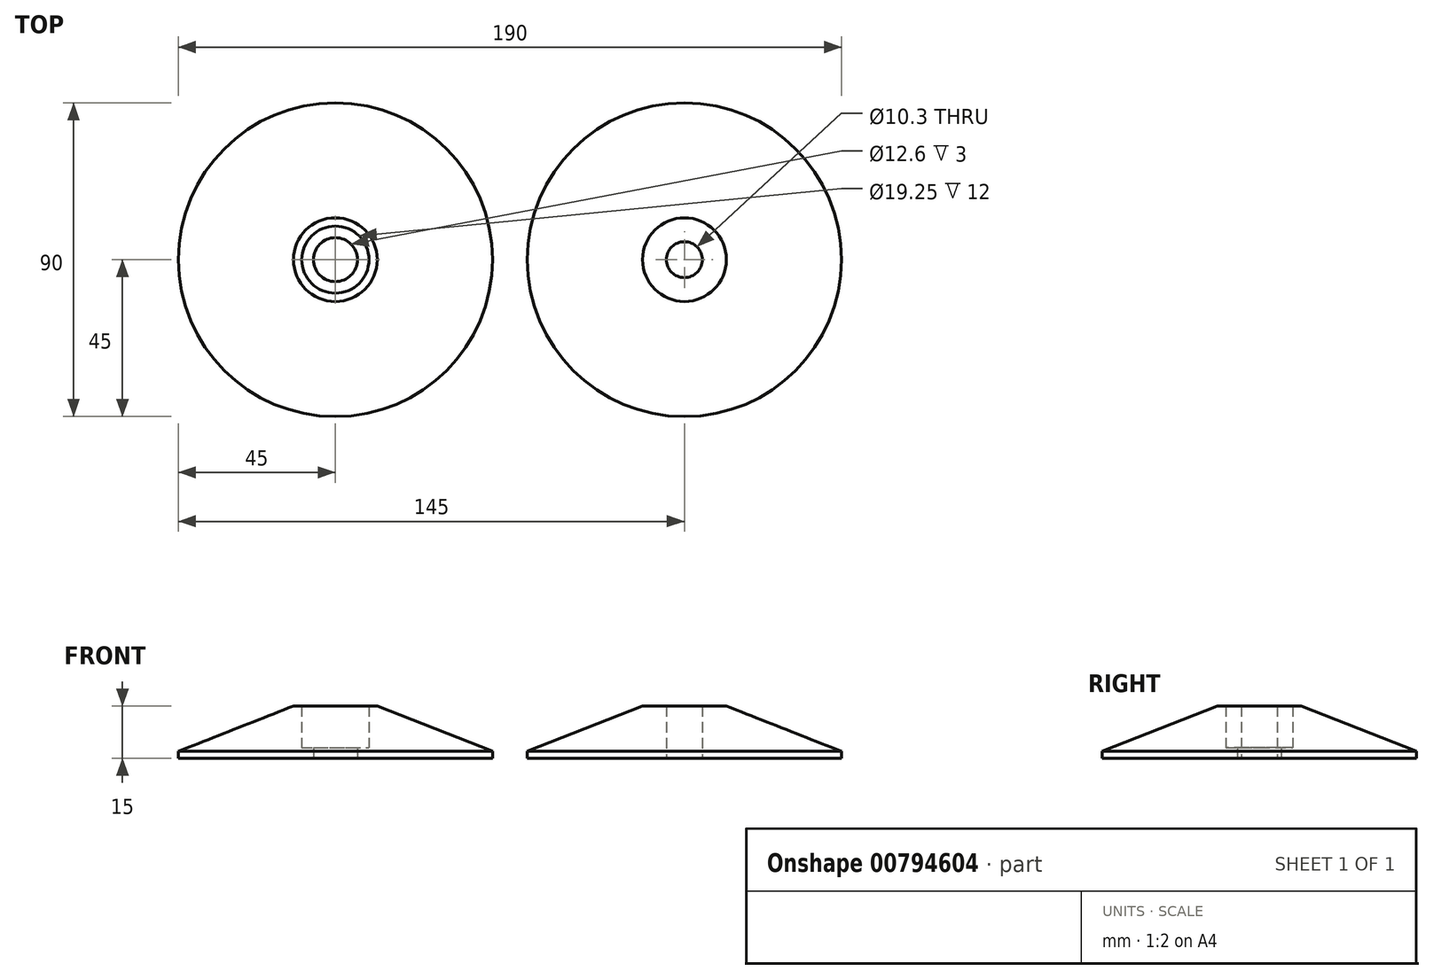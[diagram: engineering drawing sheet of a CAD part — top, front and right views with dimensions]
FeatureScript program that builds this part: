
annotation { "Feature Type Name" : "Feature", "Feature Type Description" : "" }
export const myFeature = defineFeature(function(context is Context, id is Id, definition is map)
    precondition{}
    {
        {
            var Q0;
            Q0=qCreatedBy(makeId("Front.planeOp"),FACE);
            var sketch = newSketch(context, id + "F0", { "sketchPlane" : qUnion([Q0])});
            skLineSegment(sketch, "E0", {"start": v(0, 0) * mm, "end": v(0, 21.42) * mm, "construction": true});
            skLineSegment(sketch, "E1", {"start": v(0, 0) * mm, "end": v(45, 0) * mm});
            skLineSegment(sketch, "E2", {"start": v(45, 0) * mm, "end": v(45, 2) * mm});
            skLineSegment(sketch, "E3", {"start": v(45, 2) * mm, "end": v(12, 15) * mm});
            skLineSegment(sketch, "E4", {"start": v(12, 15) * mm, "end": v(0, 15) * mm});
            skLineSegment(sketch, "E5", {"start": v(0, 15) * mm, "end": v(0, 0) * mm});
            skSolve(sketch);
        }
        {
            var Q0;
            Q0 = qSketchRegion(id + "F0", true);
            var Q1;
            Q1=sQuery(id+"F0.wireOp",EDGE,"E0");
            revolve(context, id + "F1", {"surfaceOperationType" : NewSurfaceOperationType.NEW, "entities" : qUnion([Q0]), "axis" : qUnion([Q1]), "revolveType" : RevolveType.FULL});
        }
        {
            var Q0;
            Q0=makeQuery(id+"F1.opRevolve","SWEPT_FACE",FACE,{"disambiguationData":[OSD([sQuery(id+"F0.wireOp",EDGE,"E4")])]});
            var sketch = newSketch(context, id + "F2", { "sketchPlane" : qUnion([Q0])});
            skPoint(sketch, "E6", {"position": v(0, 0) * mm});
            skSolve(sketch);
        }
        {
            var Q0;
            Q0=sQuery(id+"F2.wireOp",VERTEX,"E6");
            var Q1;
            Q1=makeQuery(id+"F1.opRevolve","SWEPT_BODY",BODY,{"disambiguationData":[OSD([sQuery(id+"F0.wireOp",EDGE,"E1"),sQuery(id+"F0.wireOp",EDGE,"E2"),sQuery(id+"F0.wireOp",EDGE,"E3"),sQuery(id+"F0.wireOp",EDGE,"E4"),sQuery(id+"F0.wireOp",EDGE,"E5")])]});
            hole(context, id + "F3", {"style" : HoleStyle.C_BORE, "endStyle" : HoleEndStyle.THROUGH, "standardTappedOrClearance" : lookupTablePath({ "standard" : "ISO", "fit" : "Close", "size" : "M12", "type" : "Clearance" }), "standardBlindInLast" : lookupTablePath({ "fit" : "Close", "standard" : "ISO", "size" : "M12", "type" : "Clearance" }), "holeDiameter" : 12.6 * mm, "cBoreDiameter" : 19.25 * mm, "cBoreDepth" : 12 * mm, "majorDiameter" : 5 * mm, "isTappedThrough" : true, "tappedDepth" : 10.5 * mm, "tapClearance" : 3, "locations" : qUnion([Q0]), "scope" : qUnion([Q1]), "startStyle" : HoleStartStyle.SKETCH});
        }
        {
            var Q0;
            Q0=makeQuery(id+"F1.opRevolve","SWEPT_BODY",BODY,{"disambiguationData":[OSD([sQuery(id+"F0.wireOp",EDGE,"E1"),sQuery(id+"F0.wireOp",EDGE,"E2"),sQuery(id+"F0.wireOp",EDGE,"E3"),sQuery(id+"F0.wireOp",EDGE,"E4"),sQuery(id+"F0.wireOp",EDGE,"E5")])]});
            transform(context, id + "F4", {"entities" : qUnion([Q0]), "transformType" : TransformType.TRANSLATION_3D, "dx" : 100 * mm, "dy" : 0 * mm, "dz" : 0 * mm, "makeCopy" : true});
        }
        {
            var Q0;
            Q0=makeQuery(id+"F4.opPattern","COPY",BODY,{"derivedFrom":makeQuery(id+"F1.opRevolve","SWEPT_BODY",BODY,{"disambiguationData":[OSD([sQuery(id+"F0.wireOp",EDGE,"E1"),sQuery(id+"F0.wireOp",EDGE,"E2"),sQuery(id+"F0.wireOp",EDGE,"E3"),sQuery(id+"F0.wireOp",EDGE,"E4"),sQuery(id+"F0.wireOp",EDGE,"E5")])]}),"instanceName":"1"});
            deleteBodies(context, id + "F5", {"entities" : qUnion([Q0])});
        }
        {
            var Q0;
            Q0=qCreatedBy(makeId("Front.planeOp"),FACE);
            var sketch = newSketch(context, id + "F6", { "sketchPlane" : qUnion([Q0])});
            skPoint(sketch, "E7", {"position": v(0, 0) * mm});
            skPoint(sketch, "E8", {"position": v(100, 0) * mm});
            skLineSegment(sketch, "E9", {"start": v(100, 0) * mm, "end": v(100, 15) * mm, "construction": true});
            skLineSegment(sketch, "E10", {"start": v(100, 0) * mm, "end": v(145, 0) * mm});
            skLineSegment(sketch, "E11", {"start": v(145, 0) * mm, "end": v(145, 2) * mm});
            skLineSegment(sketch, "E12", {"start": v(145, 2) * mm, "end": v(112, 15) * mm});
            skLineSegment(sketch, "E13", {"start": v(112, 15) * mm, "end": v(100, 15) * mm});
            skLineSegment(sketch, "E14", {"start": v(100, 15) * mm, "end": v(100, 0) * mm});
            skSolve(sketch);
        }
        {
            var Q0;
            Q0 = qSketchRegion(id + "F6", true);
            var Q1;
            Q1=sQuery(id+"F6.wireOp",EDGE,"E14");
            revolve(context, id + "F7", {"surfaceOperationType" : NewSurfaceOperationType.NEW, "entities" : qUnion([Q0]), "axis" : qUnion([Q1]), "revolveType" : RevolveType.FULL});
        }
        {
            var Q0;
            Q0=makeQuery(id+"F7.opRevolve","SWEPT_FACE",FACE,{"disambiguationData":[OSD([sQuery(id+"F6.wireOp",EDGE,"E13")])]});
            var sketch = newSketch(context, id + "F8", { "sketchPlane" : qUnion([Q0])});
            skPoint(sketch, "E15", {"position": v(100, 0) * mm});
            skSolve(sketch);
        }
        {
            var Q0;
            Q0=sQuery(id+"F8.wireOp",VERTEX,"E15");
            var Q1;
            Q1=makeQuery(id+"F7.opRevolve","SWEPT_BODY",BODY,{"disambiguationData":[OSD([sQuery(id+"F6.wireOp",EDGE,"E10"),sQuery(id+"F6.wireOp",EDGE,"E11"),sQuery(id+"F6.wireOp",EDGE,"E12"),sQuery(id+"F6.wireOp",EDGE,"E13"),sQuery(id+"F6.wireOp",EDGE,"E14")])]});
            hole(context, id + "F9", {"style" : HoleStyle.SIMPLE, "endStyle" : HoleEndStyle.THROUGH, "standardTappedOrClearance" : lookupTablePath({ "standard" : "ISO", "engagement" : "75%", "pitch" : "1.75 mm", "size" : "M12", "type" : "Tapped" }), "standardBlindInLast" : lookupTablePath({ "standard" : "ISO", "engagement" : "75%", "pitch" : "1.75 mm", "size" : "M12", "type" : "Tapped" }), "holeDiameter" : 10.3 * mm, "majorDiameter" : 12 * mm, "showTappedDepth" : true, "isTappedThrough" : true, "tappedDepth" : 10.5 * mm, "tapClearance" : 3, "locations" : qUnion([Q0]), "scope" : qUnion([Q1]), "startStyle" : HoleStartStyle.SKETCH});
        }
    });
